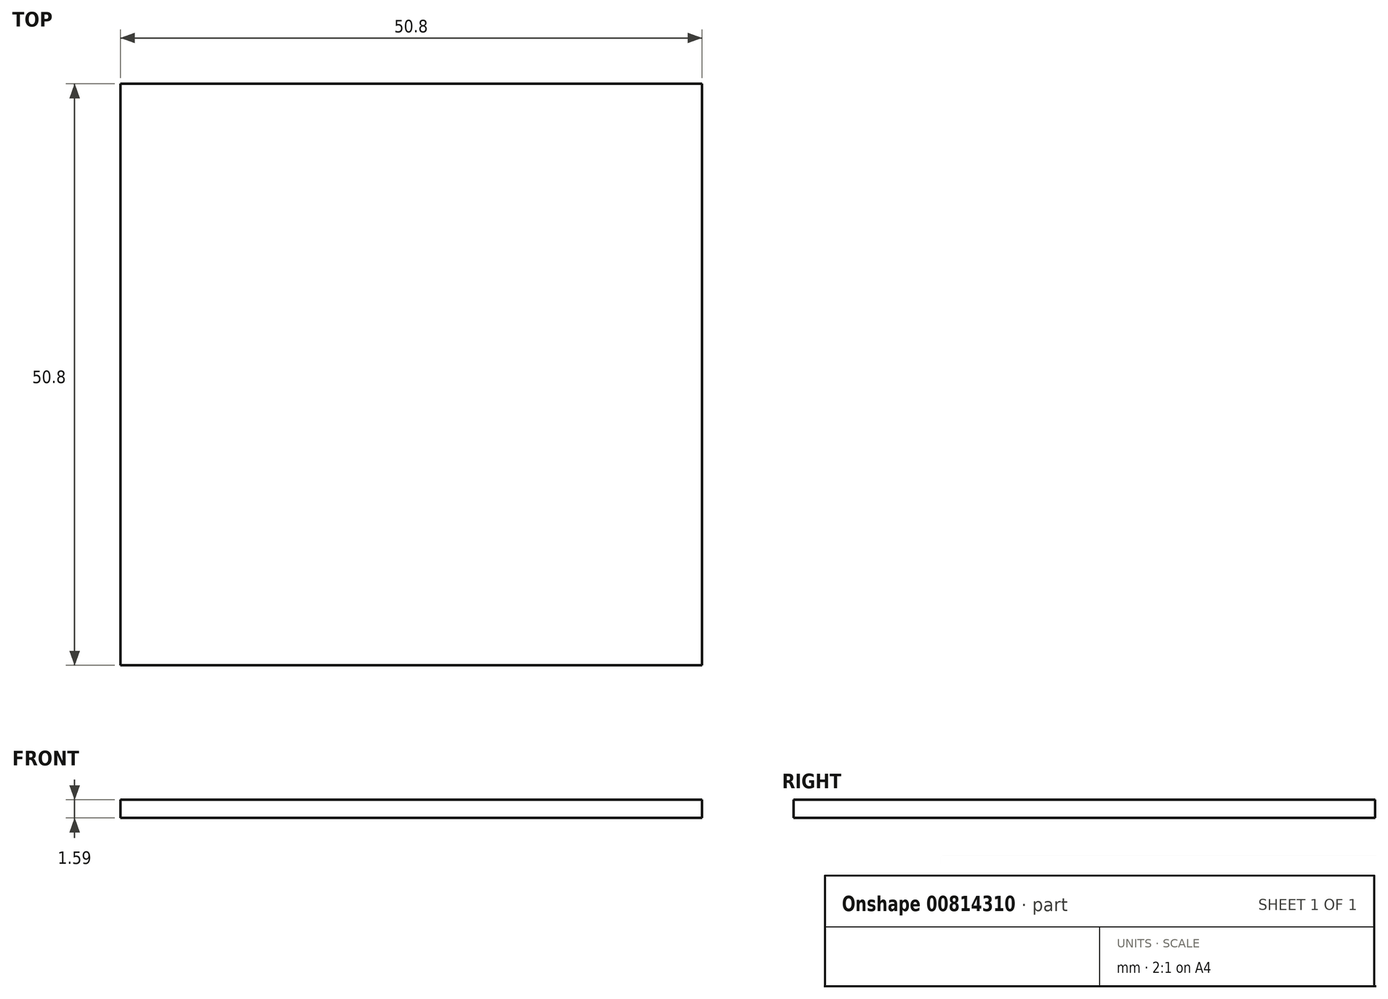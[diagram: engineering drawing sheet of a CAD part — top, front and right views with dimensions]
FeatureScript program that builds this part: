
annotation { "Feature Type Name" : "Feature", "Feature Type Description" : "" }
export const myFeature = defineFeature(function(context is Context, id is Id, definition is map)
    precondition{}
    {
        {
            var Q0;
            Q0=qCreatedBy(makeId("Top.planeOp"),FACE);
            var sketch = newSketch(context, id + "F0", { "sketchPlane" : qUnion([Q0])});
            skLineSegment(sketch, "E0.bottom", {"start": v(-25.4, 25.4) * mm, "end": v(25.4, 25.4) * mm});
            skLineSegment(sketch, "E0.top", {"start": v(-25.4, -25.4) * mm, "end": v(25.4, -25.4) * mm});
            skLineSegment(sketch, "E0.left", {"start": v(-25.4, 25.4) * mm, "end": v(-25.4, -25.4) * mm});
            skLineSegment(sketch, "E0.right", {"start": v(25.4, 25.4) * mm, "end": v(25.4, -25.4) * mm});
            skPoint(sketch, "E0.middle", {"position": v(0, 0) * mm});
            skSolve(sketch);
        }
        {
            var Q0;
            Q0=qSketchRegion(id+"F0",true);
            extrude(context, id + "F1", {"entities" : qUnion([Q0]), "depth" : 1.59 * mm, "offsetDistance" : 25.4 * mm});
        }
    });
